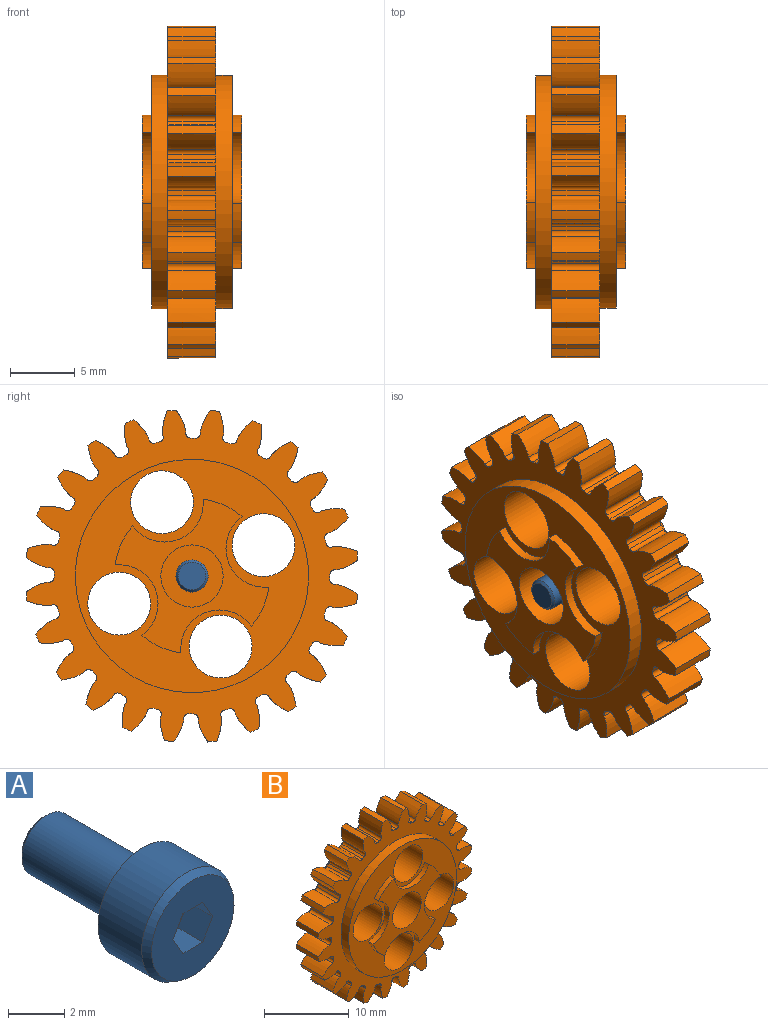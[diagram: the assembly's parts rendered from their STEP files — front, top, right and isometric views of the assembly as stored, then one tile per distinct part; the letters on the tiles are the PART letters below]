
ASSEMBLY  parts=2 mates=1
PART A: 19 faces, bbox 4.5x7.5x4.5 mm
  f0: plane 4.14x4.14mm, normal (0,-1,0), area 10.8mm2, adj f3,f10,f11,f12,f13,f14,f15
  f1: cylinder r=2.25mm len=4.5mm, axis (0,1,0), area 30.9mm2, adj f2,f3
  f2: plane 4.5x4.5mm, normal (0,1,0), area 11.1mm2, adj f1,f16
  f3: cone r=2.25mm half-angle=30deg, axis (0,1,0), area 4.9mm2, adj f0,f1
  f4: plane 1x0.87mm, normal (-0.12,-0.99,0.07), area 0.4mm2, adj f5,f9,f12
  f5: plane 1x0.87mm, normal (0,-0.99,0.14), area 0.4mm2, adj f4,f6,f13
  f6: plane 1x0.87mm, normal (0.12,-0.99,0.07), area 0.4mm2, adj f5,f7,f14
  f7: plane 1x0.87mm, normal (0.12,-0.99,-0.07), area 0.4mm2, adj f6,f8,f15
  f8: plane 1x0.87mm, normal (0,-0.99,-0.14), area 0.4mm2, adj f7,f9,f10
  f9: plane 1x0.87mm, normal (-0.12,-0.99,-0.07), area 0.4mm2, adj f4,f8,f11
  f10: plane 1.25x1mm, normal (0,0,-1), area 1.2mm2, adj f0,f8,f11,f15
  f11: plane 1.25x0.87mm, normal (-0.87,0,-0.5), area 1.3mm2, adj f0,f9,f10,f12
  f12: plane 1.25x0.87mm, normal (-0.87,0,0.5), area 1.3mm2, adj f0,f4,f11,f13
  f13: plane 1.25x1mm, normal (0,0,1), area 1.2mm2, adj f0,f5,f12,f14
  f14: plane 1.25x0.87mm, normal (0.87,0,0.5), area 1.3mm2, adj f0,f6,f13,f15
  f15: plane 1.25x0.87mm, normal (0.87,0,-0.5), area 1.3mm2, adj f0,f7,f10,f14
  f16: cylinder r=1.24mm len=4.83mm, axis (0,-1,0), area 37.6mm2, adj f2,f18
  f17: plane 2.13x2.13mm, normal (0,1,0), area 3.6mm2, adj f18
  f18: cone r=1.07mm half-angle=45deg, axis (0,-1,0), area 1.8mm2, adj f16,f17
PART B: 177 faces, bbox 25.6x7.7x25.6 mm
  f0: cylinder r=1.2mm len=2.4mm, axis (0,1,0), area 6.8mm2, adj f163,f176
  f1: cylinder r=2.43mm len=6.25mm, axis (0,-1,0), area 95.2mm2, adj f160,f169
  f2: cylinder r=2.43mm len=6.25mm, axis (0,-1,0), area 95.2mm2, adj f160,f169
  f3: cylinder r=2.43mm len=6.25mm, axis (0,-1,0), area 95.2mm2, adj f160,f169
  f4: cylinder r=2.43mm len=6.25mm, axis (0,-1,0), area 95.2mm2, adj f160,f169
  f5: cylinder r=6mm len=2.68mm, axis (0,-1,0), area 2.4mm2, adj f169,f170,f172,f174
  f6: cylinder r=6mm len=2.68mm, axis (0,-1,0), area 2.4mm2, adj f169,f170,f171,f174
  f7: cylinder r=6mm len=2.68mm, axis (0,-1,0), area 2.4mm2, adj f169,f170,f171,f173
  f8: cylinder r=6mm len=2.68mm, axis (0,-1,0), area 2.4mm2, adj f169,f170,f172,f173
  f9: plane 25.61x25.61mm, normal (0,1,0), area 181.8mm2, adj f14,f15,f16,f17,f18,f19,f20,f21
  f10: cylinder r=6mm len=2.68mm, axis (0,1,0), area 2.4mm2, adj f160,f161,f164,f167
  f11: cylinder r=6mm len=2.68mm, axis (0,1,0), area 2.4mm2, adj f160,f161,f164,f165
  f12: cylinder r=6mm len=2.68mm, axis (0,1,0), area 2.4mm2, adj f160,f161,f165,f166
  f13: cylinder r=6mm len=2.68mm, axis (0,1,0), area 2.4mm2, adj f160,f161,f166,f167
  f14: extruded ~3.7x1.82mm, area 7.4mm2, adj f9,f109,f110,f111
  f15: cylinder r=10.64mm len=3.7mm, axis (0,1,0), area 1.4mm2, adj f9,f110,f111,f112
  f16: extruded ~3.7x1.82mm, area 7.4mm2, adj f9,f17,f110,f112
  f17: cylinder r=12.87mm len=3.7mm, axis (0,1,0), area 2.6mm2, adj f9,f16,f18,f110
  f18: extruded ~3.7x1.96mm, area 7.4mm2, adj f9,f17,f110,f113
  f19: cylinder r=10.64mm len=3.7mm, axis (0,1,0), area 1.4mm2, adj f9,f110,f113,f114
  f20: extruded ~3.7x1.56mm, area 7.4mm2, adj f9,f21,f110,f114
  f21: cylinder r=12.87mm len=3.7mm, axis (0,1,0), area 2.6mm2, adj f9,f20,f22,f110
  f22: extruded ~3.7x1.96mm, area 7.4mm2, adj f9,f21,f110,f115
  f23: cylinder r=10.64mm len=3.7mm, axis (0,1,0), area 1.4mm2, adj f9,f110,f115,f116
  f24: extruded ~3.7x1.58mm, area 7.4mm2, adj f9,f25,f110,f116
  f25: cylinder r=12.87mm len=3.7mm, axis (0,1,0), area 2.6mm2, adj f9,f24,f26,f110
  f26: extruded ~3.7x1.83mm, area 7.4mm2, adj f9,f25,f110,f117
  f27: cylinder r=10.64mm len=3.7mm, axis (0,1,0), area 1.4mm2, adj f9,f110,f117,f118
  f28: extruded ~3.7x1.83mm, area 7.4mm2, adj f9,f29,f110,f118
  f29: cylinder r=12.87mm len=3.7mm, axis (0,1,0), area 2.6mm2, adj f9,f28,f30,f110
  f30: extruded ~3.7x1.58mm, area 7.4mm2, adj f9,f29,f110,f119
  f31: cylinder r=10.64mm len=3.7mm, axis (0,1,0), area 1.4mm2, adj f9,f110,f119,f120
  f32: extruded ~3.7x1.96mm, area 7.4mm2, adj f9,f33,f110,f120
  f33: cylinder r=12.87mm len=3.7mm, axis (0,1,0), area 2.6mm2, adj f9,f32,f34,f110
  f34: extruded ~3.7x1.56mm, area 7.4mm2, adj f9,f33,f110,f121
  f35: cylinder r=10.64mm len=3.7mm, axis (0,1,0), area 1.4mm2, adj f9,f110,f121,f122
  f36: extruded ~3.7x1.96mm, area 7.4mm2, adj f9,f37,f110,f122
  f37: cylinder r=12.87mm len=3.7mm, axis (0,1,0), area 2.6mm2, adj f9,f36,f38,f110
  f38: extruded ~3.7x1.82mm, area 7.4mm2, adj f9,f37,f110,f123
  f39: cylinder r=10.64mm len=3.7mm, axis (0,1,0), area 1.4mm2, adj f9,f110,f123,f124
  f40: extruded ~3.7x1.82mm, area 7.4mm2, adj f9,f41,f110,f124
  f41: cylinder r=12.87mm len=3.7mm, axis (0,1,0), area 2.6mm2, adj f9,f40,f42,f110
  f42: extruded ~3.7x1.96mm, area 7.4mm2, adj f9,f41,f110,f125
  f43: cylinder r=10.64mm len=3.7mm, axis (0,1,0), area 1.4mm2, adj f9,f110,f125,f126
  f44: extruded ~3.7x1.56mm, area 7.4mm2, adj f9,f45,f110,f126
  f45: cylinder r=12.87mm len=3.7mm, axis (0,1,0), area 2.6mm2, adj f9,f44,f46,f110
  f46: extruded ~3.7x1.96mm, area 7.4mm2, adj f9,f45,f110,f127
  f47: cylinder r=10.64mm len=3.7mm, axis (0,1,0), area 1.4mm2, adj f9,f110,f127,f128
  f48: extruded ~3.7x1.58mm, area 7.4mm2, adj f9,f49,f110,f128
  f49: cylinder r=12.87mm len=3.7mm, axis (0,1,0), area 2.6mm2, adj f9,f48,f50,f110
  f50: extruded ~3.7x1.83mm, area 7.4mm2, adj f9,f49,f110,f129
  f51: cylinder r=10.64mm len=3.7mm, axis (0,1,0), area 1.4mm2, adj f9,f110,f129,f130
  f52: extruded ~3.7x1.83mm, area 7.4mm2, adj f9,f53,f110,f130
  f53: cylinder r=12.87mm len=3.7mm, axis (0,1,0), area 2.6mm2, adj f9,f52,f54,f110
  f54: extruded ~3.7x1.58mm, area 7.4mm2, adj f9,f53,f110,f131
  f55: cylinder r=10.64mm len=3.7mm, axis (0,1,0), area 1.4mm2, adj f9,f110,f131,f132
  f56: extruded ~3.7x1.96mm, area 7.4mm2, adj f9,f57,f110,f132
  f57: cylinder r=12.87mm len=3.7mm, axis (0,1,0), area 2.6mm2, adj f9,f56,f58,f110
  f58: extruded ~3.7x1.56mm, area 7.4mm2, adj f9,f57,f110,f133
  f59: cylinder r=10.64mm len=3.7mm, axis (0,1,0), area 1.4mm2, adj f9,f110,f133,f134
  f60: extruded ~3.7x1.96mm, area 7.4mm2, adj f9,f61,f110,f134
  f61: cylinder r=12.87mm len=3.7mm, axis (0,1,0), area 2.6mm2, adj f9,f60,f62,f110
  f62: extruded ~3.7x1.82mm, area 7.4mm2, adj f9,f61,f110,f135
  f63: cylinder r=10.64mm len=3.7mm, axis (0,1,0), area 1.4mm2, adj f9,f110,f135,f136
  f64: extruded ~3.7x1.82mm, area 7.4mm2, adj f9,f65,f110,f136
  f65: cylinder r=12.87mm len=3.7mm, axis (0,1,0), area 2.6mm2, adj f9,f64,f66,f110
  f66: extruded ~3.7x1.96mm, area 7.4mm2, adj f9,f65,f110,f137
  f67: cylinder r=10.64mm len=3.7mm, axis (0,1,0), area 1.4mm2, adj f9,f110,f137,f138
  f68: extruded ~3.7x1.56mm, area 7.4mm2, adj f9,f69,f110,f138
  f69: cylinder r=12.87mm len=3.7mm, axis (0,1,0), area 2.6mm2, adj f9,f68,f70,f110
  f70: extruded ~3.7x1.96mm, area 7.4mm2, adj f9,f69,f110,f139
  f71: cylinder r=10.64mm len=3.7mm, axis (0,1,0), area 1.4mm2, adj f9,f110,f139,f140
  f72: extruded ~3.7x1.58mm, area 7.4mm2, adj f9,f73,f110,f140
  f73: cylinder r=12.87mm len=3.7mm, axis (0,1,0), area 2.6mm2, adj f9,f72,f74,f110
  f74: extruded ~3.7x1.83mm, area 7.4mm2, adj f9,f73,f110,f141
  f75: cylinder r=10.64mm len=3.7mm, axis (0,1,0), area 1.4mm2, adj f9,f110,f141,f142
  f76: extruded ~3.7x1.83mm, area 7.4mm2, adj f9,f77,f110,f142
  f77: cylinder r=12.87mm len=3.7mm, axis (0,1,0), area 2.6mm2, adj f9,f76,f78,f110
  f78: extruded ~3.7x1.58mm, area 7.4mm2, adj f9,f77,f110,f143
  f79: cylinder r=10.64mm len=3.7mm, axis (0,1,0), area 1.4mm2, adj f9,f110,f143,f144
  f80: extruded ~3.7x1.96mm, area 7.4mm2, adj f9,f81,f110,f144
  f81: cylinder r=12.87mm len=3.7mm, axis (0,1,0), area 2.6mm2, adj f9,f80,f82,f110
  f82: extruded ~3.7x1.56mm, area 7.4mm2, adj f9,f81,f110,f145
  f83: cylinder r=10.64mm len=3.7mm, axis (0,1,0), area 1.4mm2, adj f9,f110,f145,f146
  f84: extruded ~3.7x1.96mm, area 7.4mm2, adj f9,f85,f110,f146
  f85: cylinder r=12.87mm len=3.7mm, axis (0,1,0), area 2.6mm2, adj f9,f84,f86,f110
  f86: extruded ~3.7x1.82mm, area 7.4mm2, adj f9,f85,f110,f147
  f87: cylinder r=10.64mm len=3.7mm, axis (0,1,0), area 1.4mm2, adj f9,f110,f147,f148
  f88: extruded ~3.7x1.82mm, area 7.4mm2, adj f9,f89,f110,f148
  f89: cylinder r=12.87mm len=3.7mm, axis (0,1,0), area 2.6mm2, adj f9,f88,f90,f110
  f90: extruded ~3.7x1.96mm, area 7.4mm2, adj f9,f89,f110,f149
  f91: cylinder r=10.64mm len=3.7mm, axis (0,1,0), area 1.4mm2, adj f9,f110,f149,f150
  f92: extruded ~3.7x1.56mm, area 7.4mm2, adj f9,f93,f110,f150
  f93: cylinder r=12.87mm len=3.7mm, axis (0,1,0), area 2.6mm2, adj f9,f92,f94,f110
  f94: extruded ~3.7x1.96mm, area 7.4mm2, adj f9,f93,f110,f151
  f95: cylinder r=10.64mm len=3.7mm, axis (0,1,0), area 1.4mm2, adj f9,f110,f151,f152
  f96: extruded ~3.7x1.58mm, area 7.4mm2, adj f9,f97,f110,f152
  f97: cylinder r=12.87mm len=3.7mm, axis (0,1,0), area 2.6mm2, adj f9,f96,f98,f110
  f98: extruded ~3.7x1.83mm, area 7.4mm2, adj f9,f97,f110,f153
  f99: cylinder r=10.64mm len=3.7mm, axis (0,1,0), area 1.4mm2, adj f9,f110,f153,f154
  f100: extruded ~3.7x1.83mm, area 7.4mm2, adj f9,f101,f110,f154
  f101: cylinder r=12.87mm len=3.7mm, axis (0,1,0), area 2.6mm2, adj f9,f100,f102,f110
  f102: extruded ~3.7x1.58mm, area 7.4mm2, adj f9,f101,f110,f155
  f103: cylinder r=10.64mm len=3.7mm, axis (0,1,0), area 1.4mm2, adj f9,f110,f155,f156
  f104: extruded ~3.7x1.96mm, area 7.4mm2, adj f9,f105,f110,f156
  f105: cylinder r=12.87mm len=3.7mm, axis (0,1,0), area 2.6mm2, adj f9,f104,f106,f110
  f106: extruded ~3.7x1.56mm, area 7.4mm2, adj f9,f105,f110,f157
  f107: cylinder r=10.64mm len=3.7mm, axis (0,1,0), area 1.4mm2, adj f9,f110,f157,f158
  f108: extruded ~3.7x1.96mm, area 7.4mm2, adj f9,f109,f110,f158
  f109: cylinder r=12.87mm len=3.7mm, axis (0,1,0), area 2.6mm2, adj f9,f14,f108,f110
  f110: plane 25.61x25.61mm, normal (0,-1,0), area 181.8mm2, adj f14,f15,f16,f17,f18,f19,f20,f21
  f111: cylinder r=0.36mm len=3.7mm, axis (0,1,0), area 2mm2, adj f9,f14,f15,f110
  f112: cylinder r=0.36mm len=3.7mm, axis (0,1,0), area 2mm2, adj f9,f15,f16,f110
  f113: cylinder r=0.36mm len=3.7mm, axis (0,1,0), area 2mm2, adj f9,f18,f19,f110
  f114: cylinder r=0.36mm len=3.7mm, axis (0,1,0), area 2mm2, adj f9,f19,f20,f110
  f115: cylinder r=0.36mm len=3.7mm, axis (0,1,0), area 2mm2, adj f9,f22,f23,f110
  f116: cylinder r=0.36mm len=3.7mm, axis (0,1,0), area 2mm2, adj f9,f23,f24,f110
  f117: cylinder r=0.36mm len=3.7mm, axis (0,1,0), area 2mm2, adj f9,f26,f27,f110
  f118: cylinder r=0.36mm len=3.7mm, axis (0,1,0), area 2mm2, adj f9,f27,f28,f110
  f119: cylinder r=0.36mm len=3.7mm, axis (0,1,0), area 2mm2, adj f9,f30,f31,f110
  f120: cylinder r=0.36mm len=3.7mm, axis (0,1,0), area 2mm2, adj f9,f31,f32,f110
  f121: cylinder r=0.36mm len=3.7mm, axis (0,1,0), area 2mm2, adj f9,f34,f35,f110
  f122: cylinder r=0.36mm len=3.7mm, axis (0,1,0), area 2mm2, adj f9,f35,f36,f110
  f123: cylinder r=0.36mm len=3.7mm, axis (0,1,0), area 2mm2, adj f9,f38,f39,f110
  f124: cylinder r=0.36mm len=3.7mm, axis (0,1,0), area 2mm2, adj f9,f39,f40,f110
  f125: cylinder r=0.36mm len=3.7mm, axis (0,1,0), area 2mm2, adj f9,f42,f43,f110
  f126: cylinder r=0.36mm len=3.7mm, axis (0,1,0), area 2mm2, adj f9,f43,f44,f110
  f127: cylinder r=0.36mm len=3.7mm, axis (0,1,0), area 2mm2, adj f9,f46,f47,f110
  f128: cylinder r=0.36mm len=3.7mm, axis (0,1,0), area 2mm2, adj f9,f47,f48,f110
  f129: cylinder r=0.36mm len=3.7mm, axis (0,1,0), area 2mm2, adj f9,f50,f51,f110
  f130: cylinder r=0.36mm len=3.7mm, axis (0,1,0), area 2mm2, adj f9,f51,f52,f110
  f131: cylinder r=0.36mm len=3.7mm, axis (0,1,0), area 2mm2, adj f9,f54,f55,f110
  f132: cylinder r=0.36mm len=3.7mm, axis (0,1,0), area 2mm2, adj f9,f55,f56,f110
  f133: cylinder r=0.36mm len=3.7mm, axis (0,1,0), area 2mm2, adj f9,f58,f59,f110
  f134: cylinder r=0.36mm len=3.7mm, axis (0,1,0), area 2mm2, adj f9,f59,f60,f110
  f135: cylinder r=0.36mm len=3.7mm, axis (0,1,0), area 2mm2, adj f9,f62,f63,f110
  f136: cylinder r=0.36mm len=3.7mm, axis (0,1,0), area 2mm2, adj f9,f63,f64,f110
  f137: cylinder r=0.36mm len=3.7mm, axis (0,1,0), area 2mm2, adj f9,f66,f67,f110
  f138: cylinder r=0.36mm len=3.7mm, axis (0,1,0), area 2mm2, adj f9,f67,f68,f110
  f139: cylinder r=0.36mm len=3.7mm, axis (0,1,0), area 2mm2, adj f9,f70,f71,f110
  f140: cylinder r=0.36mm len=3.7mm, axis (0,1,0), area 2mm2, adj f9,f71,f72,f110
  f141: cylinder r=0.36mm len=3.7mm, axis (0,1,0), area 2mm2, adj f9,f74,f75,f110
  f142: cylinder r=0.36mm len=3.7mm, axis (0,1,0), area 2mm2, adj f9,f75,f76,f110
  f143: cylinder r=0.36mm len=3.7mm, axis (0,1,0), area 2mm2, adj f9,f78,f79,f110
  f144: cylinder r=0.36mm len=3.7mm, axis (0,1,0), area 2mm2, adj f9,f79,f80,f110
  f145: cylinder r=0.36mm len=3.7mm, axis (0,1,0), area 2mm2, adj f9,f82,f83,f110
  f146: cylinder r=0.36mm len=3.7mm, axis (0,1,0), area 2mm2, adj f9,f83,f84,f110
  f147: cylinder r=0.36mm len=3.7mm, axis (0,1,0), area 2mm2, adj f9,f86,f87,f110
  f148: cylinder r=0.36mm len=3.7mm, axis (0,1,0), area 2mm2, adj f9,f87,f88,f110
  f149: cylinder r=0.36mm len=3.7mm, axis (0,1,0), area 2mm2, adj f9,f90,f91,f110
  f150: cylinder r=0.36mm len=3.7mm, axis (0,1,0), area 2mm2, adj f9,f91,f92,f110
  f151: cylinder r=0.36mm len=3.7mm, axis (0,1,0), area 2mm2, adj f9,f94,f95,f110
  f152: cylinder r=0.36mm len=3.7mm, axis (0,1,0), area 2mm2, adj f9,f95,f96,f110
  f153: cylinder r=0.36mm len=3.7mm, axis (0,1,0), area 2mm2, adj f9,f98,f99,f110
  f154: cylinder r=0.36mm len=3.7mm, axis (0,1,0), area 2mm2, adj f9,f99,f100,f110
  f155: cylinder r=0.36mm len=3.7mm, axis (0,1,0), area 2mm2, adj f9,f102,f103,f110
  f156: cylinder r=0.36mm len=3.7mm, axis (0,1,0), area 2mm2, adj f9,f103,f104,f110
  f157: cylinder r=0.36mm len=3.7mm, axis (0,1,0), area 2mm2, adj f9,f106,f107,f110
  f158: cylinder r=0.36mm len=3.7mm, axis (0,1,0), area 2mm2, adj f9,f107,f108,f110
  f159: cylinder r=9mm len=18mm, axis (0,1,0), area 70.7mm2, adj f110,f160
  f160: plane 18x18mm, normal (0,-1,0), area 117.7mm2, adj f1,f2,f3,f4,f10,f11,f12,f13
  f161: plane 11.27x11.27mm, normal (0,-1,0), area 44.8mm2, adj f10,f11,f12,f13,f162,f164,f165,f166
  f162: cylinder r=2.4mm len=4.8mm, axis (0,-1,0), area 62.6mm2, adj f161,f163
  f163: plane 4.8x4.8mm, normal (0,-1,0), area 13.6mm2, adj f0,f162
  f164: cylinder r=3mm len=5.74mm, axis (0,1,0), area 5.5mm2, adj f10,f11,f160,f161
  f165: cylinder r=3mm len=5.74mm, axis (0,1,0), area 5.5mm2, adj f11,f12,f160,f161
  f166: cylinder r=3mm len=5.74mm, axis (0,1,0), area 5.5mm2, adj f12,f13,f160,f161
  f167: cylinder r=3mm len=5.74mm, axis (0,1,0), area 5.5mm2, adj f10,f13,f160,f161
  f168: cylinder r=9mm len=18mm, axis (0,-1,0), area 73.5mm2, adj f9,f169
  f169: plane 18x18mm, normal (0,1,0), area 117.7mm2, adj f1,f2,f3,f4,f5,f6,f7,f8
  f170: plane 11.27x11.27mm, normal (0,1,0), area 43.2mm2, adj f5,f6,f7,f8,f171,f172,f173,f174
  f171: cylinder r=3mm len=5.74mm, axis (0,-1,0), area 5.5mm2, adj f6,f7,f169,f170
  f172: cylinder r=3mm len=5.74mm, axis (0,-1,0), area 5.5mm2, adj f5,f8,f169,f170
  f173: cylinder r=3mm len=5.74mm, axis (0,-1,0), area 5.5mm2, adj f7,f8,f169,f170
  f174: cylinder r=3mm len=5.74mm, axis (0,-1,0), area 5.5mm2, adj f5,f6,f169,f170
  f175: cylinder r=2.5mm len=5mm, axis (0,1,0), area 40.8mm2, adj f170,f176
  f176: plane 5x5mm, normal (0,1,0), area 15.1mm2, adj f0,f175
PLACE A rot(axis=(-0.65,0.65,0.38),138.3deg) t=(39.65,7.98,25)mm
PLACE B rot(axis=(-0.65,-0.65,-0.38),138.3deg) t=(37.75,7.98,25)mm fixed
MATE fastened A.f1 <-> B.f0  axis (-1,0,0) through (37.15,7.98,25)mm
